# Revit family: 51-SUBCJ GF LVP SENC PARED FONTANA
name_source: partatom
category: Aparatos sanitarios
revit_build: Autodesk Revit 2018 (Build: 20170223_1515(x64)
units: mm (PartAtom-declared; Revit-internal decimal feet)

## family parameters
Anfitrión = Cara
Compartido = No
Corte con vacíos al cargar = No
Cota de conector redondo = Diámetro de uso
Número OmniClass = 23.45.55.14
Punto de cálculo de habitación = No
Tipo de pieza = Normal
Título OmniClass = Single Faucets

## types (1)
- 51-SUBCJ GF LVP SENC PARED FONTANA
    Acabado = Brillante
    Accionamiento = Manual
    Ahorro de Agua = Ahorro de agua (8,3l/min.) cumple con la norma NTC 1644
    Altura Nominal = 218
    Ancho Nominal = 60
    Características = Ahorro de agua, acabado más brillante y resistente a la corrosión, pico oscilante para mayor alcance y comodidad, fácil limpieza evita acumulación de impurezas
    Caudal = 80 psi.
    Color = Cromo
    Consumo de agua = 8,3l/min.
    Código de montaje = D2010
    Descripción = Plumbing Fixtures
    Descripción IFC = Grifería sencilla Fontana
    Descripción de la garantía = Garantía de 30 años, garantía de 5 años en acabados.
    Diámetro de conexión de entrada = 1/2 Pulg.
    Duración Garantía Partes = 30
    Duración Garantía Unidad = Años
    Duración Unidad = Años
    Elevación por defecto = 0 mm  [stored 0 ft]
    Fabricante = www.corona.com.co
    Forma = Cilíndrica
    Información del producto = https://www.grival.com
    Logitud Nominal = 209
    Material Acabado = Cromo-Corona
    Material de Fabricación = Plástico
    Nombre = Grifería cocina Fontana
    Nombre del Fabricante = Corona / Grival
    Número Modelo = 517000001
    Presión Máxima = 20
    Presión mínima = 125
    Requerimientos Accesibilidad = Manual
    Responsable Garantías Partes = www.corona.com.co
    Tamaño = 209 x 60 x 218
    Tiempo Útil = 30
    Tipo de activo = Fijo
    Tráfico = Residencial
    Vida útil = Unidad de cierre 500000, pico 50000
    Vida útil unidad = Ciclos

note: [stored X ft] marks values corroborated as IEEE doubles in the binary element streams (Revit-internal decimal feet)

## geometry (parser evidence)
native form markers: Sweep x2
no freeform markers — native parametric forms only
